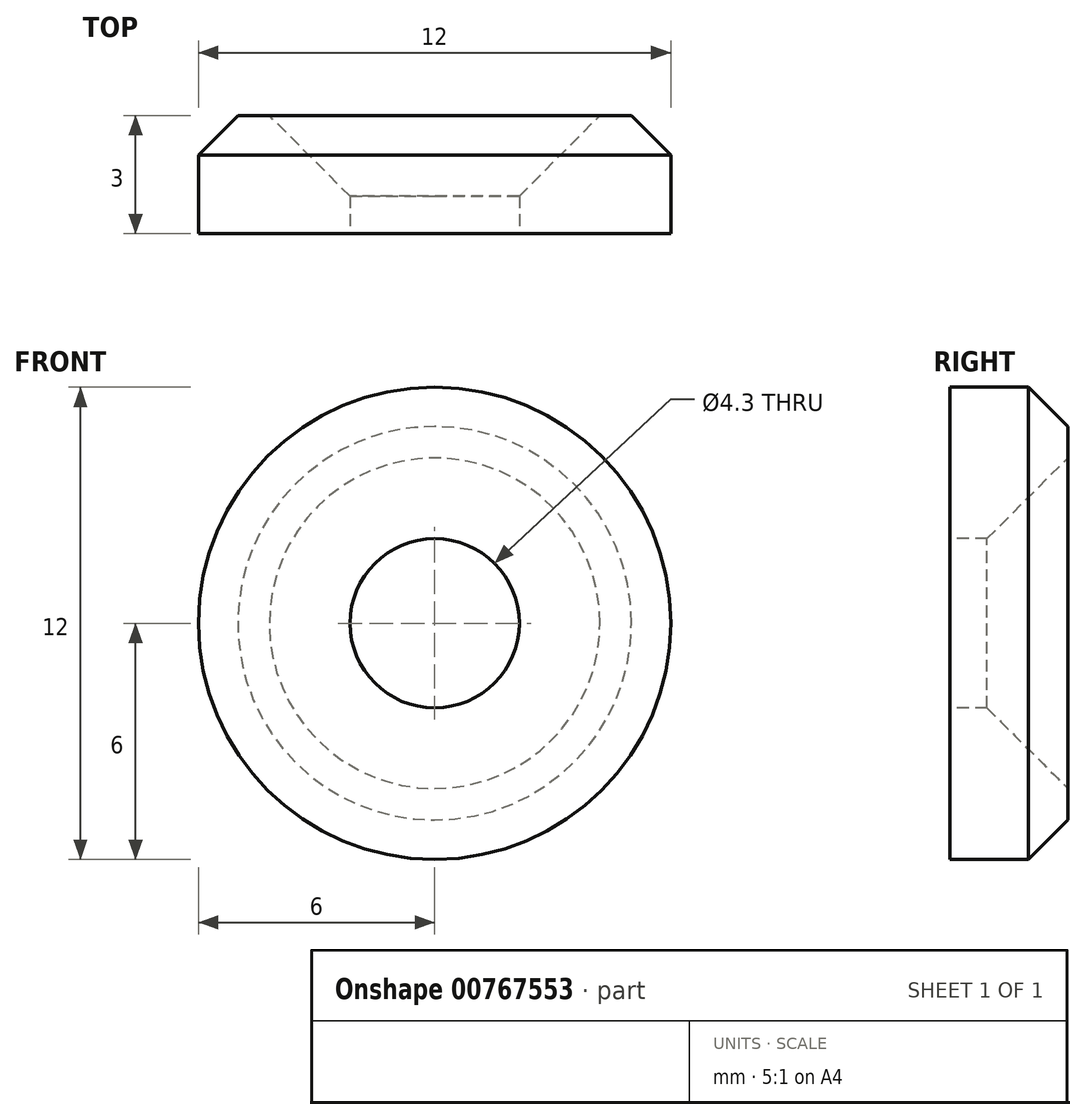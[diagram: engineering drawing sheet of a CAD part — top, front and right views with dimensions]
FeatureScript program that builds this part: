
annotation { "Feature Type Name" : "Feature", "Feature Type Description" : "" }
export const myFeature = defineFeature(function(context is Context, id is Id, definition is map)
    precondition{}
    {
        {
            var Q0;
            Q0=qCreatedBy(makeId("Right.planeOp"),FACE);
            var sketch = newSketch(context, id + "F0", { "sketchPlane" : qUnion([Q0])});
            skLineSegment(sketch, "E0", {"start": v(0, 2.15) * mm, "end": v(0.95, 2.15) * mm});
            skLineSegment(sketch, "E1", {"start": v(0.95, 2.15) * mm, "end": v(3, 4.2) * mm});
            skLineSegment(sketch, "E2", {"start": v(3, 4.2) * mm, "end": v(3, 6) * mm});
            skLineSegment(sketch, "E3", {"start": v(3, 6) * mm, "end": v(0, 6) * mm});
            skLineSegment(sketch, "E4", {"start": v(0, 6) * mm, "end": v(0, 2.15) * mm});
            skLineSegment(sketch, "E5", {"start": v(0, 0) * mm, "end": v(3, 0) * mm, "construction": true});
            skPoint(sketch, "E5.endSnap0", {"position": v(3, 5.1) * mm});
            skSolve(sketch);
        }
        {
            var Q0;
            Q0=makeQuery(id+"F0.imprint","IMPRINT",FACE,{"disambiguationData":[TD([[makeQuery(id+"F0.imprint","IMPRINT",EDGE,{"derivedFrom":sQuery(id+"F0.wireOp",EDGE,"E0")}),1.0]])]});
            var Q1;
            Q1=sQuery(id+"F0.wireOp",EDGE,"E5");
            revolve(context, id + "F1", {"surfaceOperationType" : NewSurfaceOperationType.NEW, "entities" : qUnion([Q0]), "axis" : qUnion([Q1]), "revolveType" : RevolveType.FULL});
        }
        {
            var Q0;
            Q0=makeQuery(id+"F1.opRevolve","SWEPT_EDGE",EDGE,{"disambiguationData":[OSD([sQuery(id+"F0.wireOp",EDGE,"E2"),sQuery(id+"F0.wireOp",EDGE,"E3")])]});
            chamfer(context, id + "F2", {"entities" : qUnion([Q0]), "width" : 1 * mm, "tangentPropagation" : true});
        }
    });
